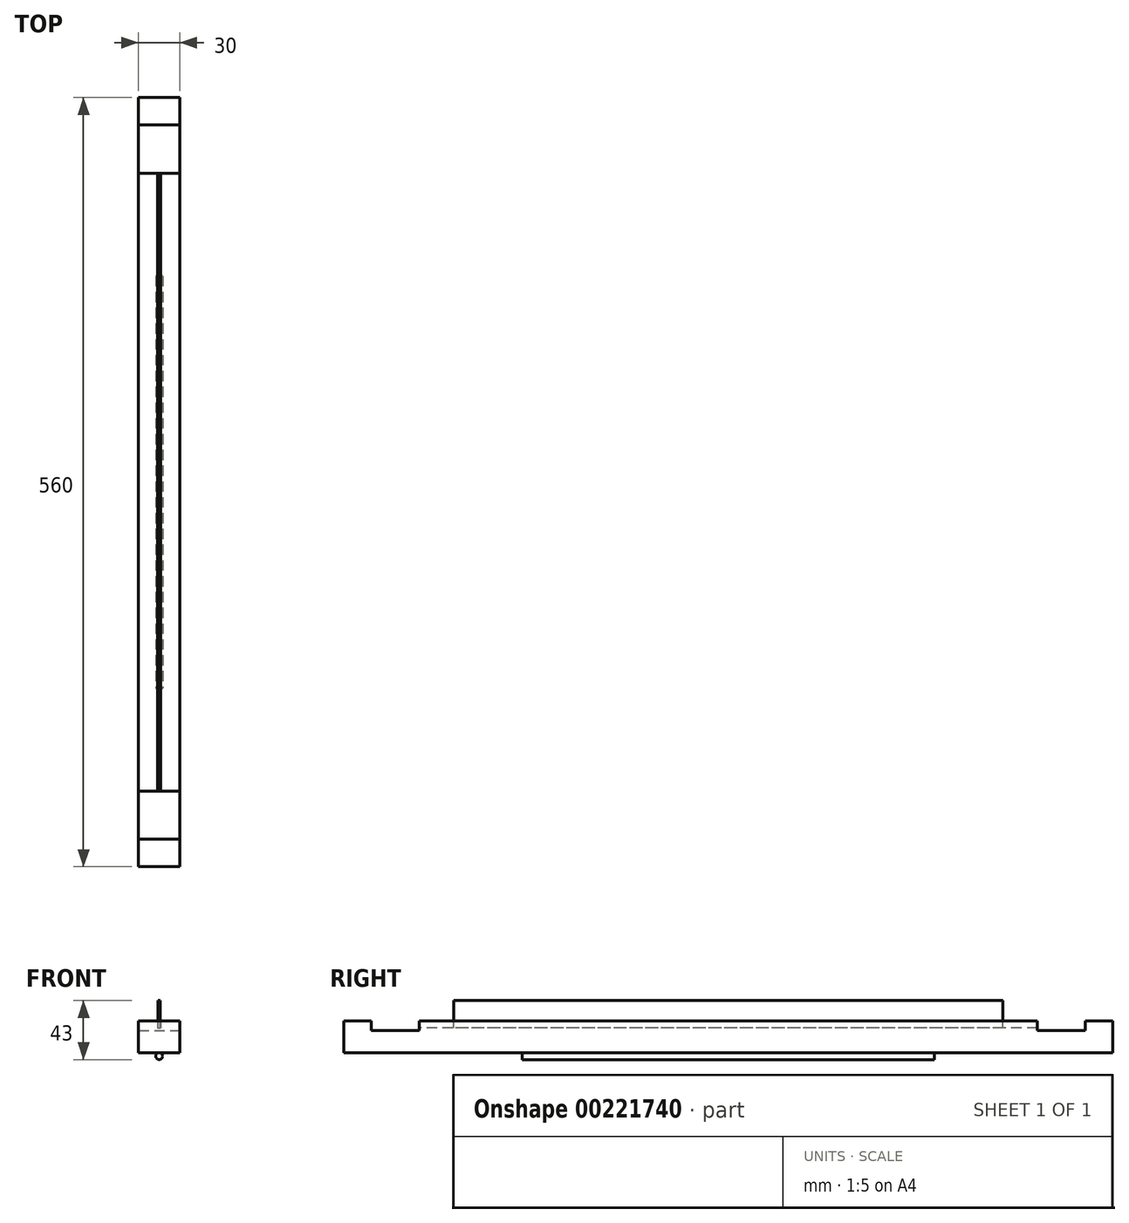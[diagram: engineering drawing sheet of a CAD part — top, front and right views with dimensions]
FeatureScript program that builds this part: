
annotation { "Feature Type Name" : "Feature", "Feature Type Description" : "" }
export const myFeature = defineFeature(function(context is Context, id is Id, definition is map)
    precondition{}
    {
        {
            var Q0;
            Q0=qCreatedBy(makeId("Front.planeOp"),FACE);
            var sketch = newSketch(context, id + "F0", { "sketchPlane" : qUnion([Q0])});
            skLineSegment(sketch, "E0.bottom", {"start": v(-15, 11.5) * mm, "end": v(15, 11.5) * mm});
            skLineSegment(sketch, "E0.top", {"start": v(-15, -11.5) * mm, "end": v(15, -11.5) * mm});
            skLineSegment(sketch, "E0.left", {"start": v(-15, 11.5) * mm, "end": v(-15, -11.5) * mm});
            skLineSegment(sketch, "E0.right", {"start": v(15, 11.5) * mm, "end": v(15, -11.5) * mm});
            skPoint(sketch, "E0.middle", {"position": v(0, 0) * mm});
            skSolve(sketch);
        }
        {
            var Q0;
            Q0 = qSketchRegion(id + "F0", true);
            extrude(context, id + "F1", {"entities" : qUnion([Q0]), "depth" : 560 * mm});
        }
        {
            var Q0;
            Q0=makeQuery(id+"F1.opExtrude","SWEPT_FACE",FACE,{"disambiguationData":[OSD([sQuery(id+"F0.wireOp",EDGE,"E0.right")])]});
            var sketch = newSketch(context, id + "F2", { "sketchPlane" : qUnion([Q0])});
            skLineSegment(sketch, "E1", {"start": v(-540, 11.5) * mm, "end": v(-540, 4.5) * mm});
            skLineSegment(sketch, "E2", {"start": v(-540, 4.5) * mm, "end": v(-505, 4.5) * mm});
            skLineSegment(sketch, "E3", {"start": v(-505, 4.5) * mm, "end": v(-505, 11.5) * mm});
            skLineSegment(sketch, "E4", {"start": v(-505, 11.5) * mm, "end": v(-540, 11.5) * mm});
            skLineSegment(sketch, "E5", {"start": v(-280, 11.5) * mm, "end": v(-280, -11.5) * mm, "construction": true});
            skLineSegment(sketch, "E6.MirrorCS", {"start": v(-20, 11.5) * mm, "end": v(-20, 4.5) * mm});
            skLineSegment(sketch, "E7.MirrorCS", {"start": v(-55, 11.5) * mm, "end": v(-20, 11.5) * mm});
            skLineSegment(sketch, "E8.MirrorCS", {"start": v(-55, 4.5) * mm, "end": v(-20, 4.5) * mm});
            skLineSegment(sketch, "E9.MirrorCS", {"start": v(-55, 4.5) * mm, "end": v(-55, 11.5) * mm});
            skSolve(sketch);
        }
        {
            var Q0;
            Q0 = qSketchRegion(id + "F2", true);
            extrude(context, id + "F3", {"entities" : qUnion([Q0]), "operationType" : NewBodyOperationType.REMOVE, "endBound" : BoundingType.THROUGH_ALL, "oppositeDirection" : true, "depth" : 25 * mm});
        }
        {
            var Q0;
            Q0=makeQuery(id+"F3.boolean.opBoolean","COPY",FACE,{"derivedFrom":makeQuery(id+"F3.opExtrude","SWEPT_FACE",FACE,{"disambiguationData":[OSD([sQuery(id+"F2.wireOp",EDGE,"E3")])]})});
            var sketch = newSketch(context, id + "F4", { "sketchPlane" : qUnion([Q0])});
            skPoint(sketch, "E10.oppositeSnap0", {"position": v(1, 6.5) * mm});
            skLineSegment(sketch, "E10.bottom", {"start": v(-1, 11.5) * mm, "end": v(1, 11.5) * mm});
            skLineSegment(sketch, "E10.top", {"start": v(-1, 6.5) * mm, "end": v(1, 6.5) * mm});
            skLineSegment(sketch, "E10.left", {"start": v(-1, 11.5) * mm, "end": v(-1, 6.5) * mm});
            skLineSegment(sketch, "E10.right", {"start": v(1, 11.5) * mm, "end": v(1, 6.5) * mm});
            skSolve(sketch);
        }
        {
            var Q0;
            Q0 = qSketchRegion(id + "F4", true);
            var Q1;
            Q1=makeQuery(id+"F3.boolean.opBoolean","COPY",FACE,{"derivedFrom":makeQuery(id+"F3.opExtrude","SWEPT_FACE",FACE,{"disambiguationData":[OSD([sQuery(id+"F2.wireOp",EDGE,"E9.MirrorCS")])]})});
            extrude(context, id + "F5", {"entities" : qUnion([Q0]), "operationType" : NewBodyOperationType.REMOVE, "endBound" : BoundingType.UP_TO_SURFACE, "oppositeDirection" : true, "endBoundEntityFace" : qUnion([Q1]), "depth" : 25 * mm});
        }
        {
            var Q0;
            Q0=makeQuery(id+"F5.boolean.opBoolean","SPLIT",FACE,{"disambiguationData":[TD([makeQuery(id+"F1.opExtrude","SWEPT_FACE",FACE,{"disambiguationData":[OSD([sQuery(id+"F0.wireOp",EDGE,"E0.right")])]})])],"derivedFrom":makeQuery(id+"F3.boolean.opBoolean","COPY",FACE,{"derivedFrom":makeQuery(id+"F3.opExtrude","SWEPT_FACE",FACE,{"disambiguationData":[OSD([sQuery(id+"F2.wireOp",EDGE,"E3")])]})})});
            var sketch = newSketch(context, id + "F6", { "sketchPlane" : qUnion([Q0])});
            skLineSegment(sketch, "E11.bottom", {"start": v(0.9, 6.5) * mm, "end": v(-0.9, 6.5) * mm});
            skLineSegment(sketch, "E11.top", {"start": v(0.9, 26.5) * mm, "end": v(-0.9, 26.5) * mm});
            skLineSegment(sketch, "E11.left", {"start": v(0.9, 6.5) * mm, "end": v(0.9, 26.5) * mm});
            skLineSegment(sketch, "E11.right", {"start": v(-0.9, 6.5) * mm, "end": v(-0.9, 26.5) * mm});
            skSolve(sketch);
        }
        {
            var Q0;
            Q0 = qSketchRegion(id + "F6", true);
            var Q1;
            Q1=makeQuery(id+"F5.boolean.opBoolean","SPLIT",FACE,{"disambiguationData":[TD([makeQuery(id+"F1.opExtrude","SWEPT_FACE",FACE,{"disambiguationData":[OSD([sQuery(id+"F0.wireOp",EDGE,"E0.left")])]})])],"derivedFrom":makeQuery(id+"F3.boolean.opBoolean","COPY",FACE,{"derivedFrom":makeQuery(id+"F3.opExtrude","SWEPT_FACE",FACE,{"disambiguationData":[OSD([sQuery(id+"F2.wireOp",EDGE,"E9.MirrorCS")])]})})});
            var Q2;
            Q2=makeQuery(id+"F1.opExtrude","SWEPT_BODY",BODY,{"disambiguationData":[OSD([sQuery(id+"F0.wireOp",EDGE,"E0.bottom"),sQuery(id+"F0.wireOp",EDGE,"E0.top"),sQuery(id+"F0.wireOp",EDGE,"E0.left"),sQuery(id+"F0.wireOp",EDGE,"E0.right")])]});
            extrude(context, id + "F7", {"entities" : qUnion([Q0]), "oppositeDirection" : true, "endBoundEntityFace" : qUnion([Q1]), "endBoundEntityBody" : qUnion([Q2]), "depth" : 425 * mm, "hasSecondDirection" : true, "secondDirectionOppositeDirection" : true, "secondDirectionDepth" : 25 * mm});
        }
        {
            var Q0;
            Q0=makeQuery(id+"F1.opExtrude","CAP_FACE",FACE,{"disambiguationData":[OSD([sQuery(id+"F0.wireOp",EDGE,"E0.bottom"),sQuery(id+"F0.wireOp",EDGE,"E0.top"),sQuery(id+"F0.wireOp",EDGE,"E0.left"),sQuery(id+"F0.wireOp",EDGE,"E0.right")])],"isStart":false});
            var sketch = newSketch(context, id + "F8", { "sketchPlane" : qUnion([Q0])});
            skCircle(sketch, "E12", {"center": v(0, -14) * mm, "radius": 2.5 * mm});
            skSolve(sketch);
        }
        {
            var Q0;
            Q0 = qSketchRegion(id + "F8", true);
            extrude(context, id + "F9", {"entities" : qUnion([Q0]), "operationType" : NewBodyOperationType.ADD, "oppositeDirection" : true, "depth" : 430 * mm, "hasSecondDirection" : true, "secondDirectionOppositeDirection" : true, "secondDirectionDepth" : 130 * mm});
        }
    });
